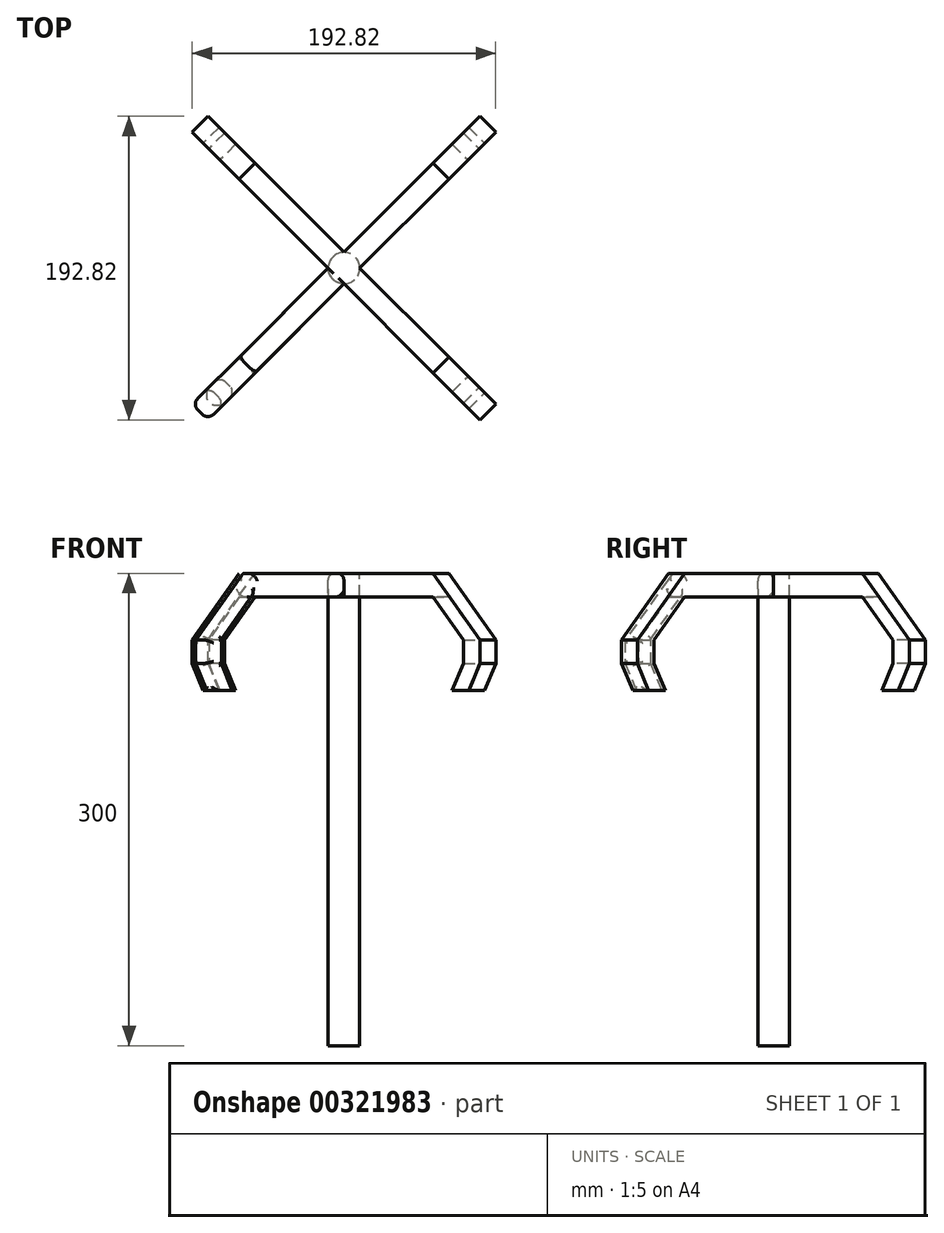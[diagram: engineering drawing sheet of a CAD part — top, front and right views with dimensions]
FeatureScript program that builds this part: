
annotation { "Feature Type Name" : "Feature", "Feature Type Description" : "" }
export const myFeature = defineFeature(function(context is Context, id is Id, definition is map)
    precondition{}
    {
        {
            var Q0;
            Q0=qCreatedBy(makeId("Top.planeOp"),FACE);
            var sketch = newSketch(context, id + "F0", { "sketchPlane" : qUnion([Q0])});
            skCircle(sketch, "E0", {"center": v(0, 0) * mm, "radius": 10 * mm});
            skSolve(sketch);
        }
        {
            var Q0;
            Q0 = qSketchRegion(id + "F0", true);
            extrude(context, id + "F1", {"entities" : qUnion([Q0]), "depth" : 300 * mm});
        }
        {
            var Q0;
            Q0=makeQuery(id+"F1.opExtrude","CAP_FACE",FACE,{"disambiguationData":[OSD([sQuery(id+"F0.wireOp",EDGE,"E0")])],"isStart":false});
            var sketch = newSketch(context, id + "F2", { "sketchPlane" : qUnion([Q0])});
            skLineSegment(sketch, "E1.bottom", {"start": v(10, 10) * mm, "end": v(-10, 10) * mm});
            skLineSegment(sketch, "E1.top", {"start": v(10, -10) * mm, "end": v(-10, -10) * mm});
            skLineSegment(sketch, "E1.left", {"start": v(10, 10) * mm, "end": v(10, -10) * mm});
            skLineSegment(sketch, "E1.right", {"start": v(-10, 10) * mm, "end": v(-10, -10) * mm});
            skPoint(sketch, "E1.middle", {"position": v(0, 0) * mm});
            skLineSegment(sketch, "E2", {"start": v(0, -10) * mm, "end": v(-56.57, -66.57) * mm});
            skLineSegment(sketch, "E3", {"start": v(-56.57, -66.57) * mm, "end": v(-66.57, -56.57) * mm});
            skLineSegment(sketch, "E4", {"start": v(-66.57, -56.57) * mm, "end": v(-10, 0) * mm});
            skLineSegment(sketch, "E5", {"start": v(-10, 0) * mm, "end": v(-66.57, 56.57) * mm});
            skLineSegment(sketch, "E6", {"start": v(-66.57, 56.57) * mm, "end": v(-56.57, 66.57) * mm});
            skLineSegment(sketch, "E7", {"start": v(-56.57, 66.57) * mm, "end": v(0, 10) * mm});
            skLineSegment(sketch, "E8", {"start": v(0, 10) * mm, "end": v(56.57, 66.57) * mm});
            skLineSegment(sketch, "E9", {"start": v(56.57, 66.57) * mm, "end": v(66.57, 56.57) * mm});
            skLineSegment(sketch, "E10", {"start": v(66.57, 56.57) * mm, "end": v(10, 0) * mm});
            skLineSegment(sketch, "E11", {"start": v(10, 0) * mm, "end": v(66.57, -56.57) * mm});
            skLineSegment(sketch, "E12", {"start": v(66.57, -56.57) * mm, "end": v(56.57, -66.57) * mm});
            skLineSegment(sketch, "E13", {"start": v(56.57, -66.57) * mm, "end": v(0, -10) * mm});
            skSolve(sketch);
        }
        {
            var Q0;
            Q0 = qSketchRegion(id + "F2", true);
            extrude(context, id + "F3", {"entities" : qUnion([Q0]), "operationType" : NewBodyOperationType.ADD, "oppositeDirection" : true, "depth" : 15 * mm});
        }
        {
            var Q0;
            Q0=makeQuery(id+"F3.opExtrude","SWEPT_FACE",FACE,{"disambiguationData":[OSD([sQuery(id+"F2.wireOp",EDGE,"E10")])]});
            var sketch = newSketch(context, id + "F4", { "sketchPlane" : qUnion([Q0])});
            skLineSegment(sketch, "E14", {"start": v(87.07, 300) * mm, "end": v(87.07, 285) * mm});
            skLineSegment(sketch, "E15", {"start": v(87.07, 285) * mm, "end": v(114.28, 257.8) * mm});
            skLineSegment(sketch, "E16", {"start": v(114.28, 257.8) * mm, "end": v(114.28, 242.8) * mm});
            skLineSegment(sketch, "E17", {"start": v(114.28, 242.8) * mm, "end": v(129.28, 242.8) * mm});
            skLineSegment(sketch, "E18", {"start": v(129.28, 242.8) * mm, "end": v(129.28, 257.8) * mm});
            skLineSegment(sketch, "E19", {"start": v(129.28, 257.8) * mm, "end": v(87.07, 300) * mm});
            skLineSegment(sketch, "E20", {"start": v(129.28, 242.8) * mm, "end": v(119.3, 225.52) * mm});
            skLineSegment(sketch, "E21", {"start": v(119.3, 225.52) * mm, "end": v(104.3, 225.52) * mm});
            skLineSegment(sketch, "E22", {"start": v(104.3, 225.52) * mm, "end": v(114.28, 242.8) * mm});
            skSolve(sketch);
        }
        {
            var Q0;
            Q0=makeQuery(id+"F4.imprint","IMPRINT",FACE,{"disambiguationData":[TD([[makeQuery(id+"F4.imprint","IMPRINT",EDGE,{"derivedFrom":sQuery(id+"F4.wireOp",EDGE,"E14")}),-1.0]])]});
            var Q1;
            Q1=makeQuery(id+"F4.imprint","IMPRINT",FACE,{"disambiguationData":[TD([[makeQuery(id+"F4.imprint","IMPRINT",EDGE,{"derivedFrom":sQuery(id+"F4.wireOp",EDGE,"E17")}),-1.0]])]});
            extrude(context, id + "F5", {"entities" : qUnion([Q0, Q1]), "operationType" : NewBodyOperationType.ADD, "oppositeDirection" : true, "depth" : 14.14 * mm});
        }
        {
            var Q0;
            Q0=makeQuery(id+"F1.opExtrude","SWEPT_BODY",BODY,{"disambiguationData":[OSD([sQuery(id+"F0.wireOp",EDGE,"E0")])]});
            var Q1;
            Q1=qCreatedBy(makeId("Front.planeOp"),FACE);
            mirror(context, id + "F6", {"operationType" : NewBodyOperationType.ADD, "entities" : qUnion([Q0]), "mirrorPlane" : qUnion([Q1])});
        }
        {
            var Q0;
            Q0=makeQuery(id+"F1.opExtrude","SWEPT_BODY",BODY,{"disambiguationData":[OSD([sQuery(id+"F0.wireOp",EDGE,"E0")])]});
            var Q1;
            Q1=qCreatedBy(makeId("Right.planeOp"),FACE);
            mirror(context, id + "F7", {"operationType" : NewBodyOperationType.ADD, "entities" : qUnion([Q0]), "mirrorPlane" : qUnion([Q1])});
        }
        {
            var Q0;
            Q0=makeQuery(id+"F3.opExtrude","CAP_EDGE",EDGE,{"disambiguationData":[OSD([sQuery(id+"F2.wireOp",EDGE,"E2")])],"isStart":true});
            var Q1;
            Q1=makeQuery(id+"F7.opPattern","COPY",EDGE,{"derivedFrom":makeQuery(id+"F6.opPattern","COPY",EDGE,{"derivedFrom":makeQuery(id+"F5.opExtrude","CAP_EDGE",EDGE,{"disambiguationData":[OSD([sQuery(id+"F4.wireOp",EDGE,"E19")])],"isStart":false}),"instanceName":"1"}),"instanceName":"1"});
            var Q2;
            Q2=makeQuery(id+"F7.opPattern","COPY",EDGE,{"derivedFrom":makeQuery(id+"F6.opPattern","COPY",EDGE,{"derivedFrom":makeQuery(id+"F5.opExtrude","CAP_EDGE",EDGE,{"disambiguationData":[OSD([sQuery(id+"F4.wireOp",EDGE,"E18")])],"isStart":false}),"instanceName":"1"}),"instanceName":"1"});
            var Q3;
            Q3=makeQuery(id+"F7.opPattern","COPY",EDGE,{"derivedFrom":makeQuery(id+"F6.opPattern","COPY",EDGE,{"derivedFrom":makeQuery(id+"F5.opExtrude","CAP_EDGE",EDGE,{"disambiguationData":[OSD([sQuery(id+"F4.wireOp",EDGE,"E20")])],"isStart":false}),"instanceName":"1"}),"instanceName":"1"});
            var Q4;
            Q4=makeQuery(id+"F3.opExtrude","CAP_EDGE",EDGE,{"disambiguationData":[OSD([sQuery(id+"F2.wireOp",EDGE,"E2")])],"isStart":false});
            var Q5;
            Q5=makeQuery(id+"F7.opPattern","COPY",EDGE,{"derivedFrom":makeQuery(id+"F6.opPattern","COPY",EDGE,{"derivedFrom":makeQuery(id+"F5.opExtrude","CAP_EDGE",EDGE,{"disambiguationData":[OSD([sQuery(id+"F4.wireOp",EDGE,"E15")])],"isStart":false}),"instanceName":"1"}),"instanceName":"1"});
            var Q6;
            Q6=makeQuery(id+"F7.opPattern","COPY",EDGE,{"derivedFrom":makeQuery(id+"F6.opPattern","COPY",EDGE,{"derivedFrom":makeQuery(id+"F5.opExtrude","CAP_EDGE",EDGE,{"disambiguationData":[OSD([sQuery(id+"F4.wireOp",EDGE,"E16")])],"isStart":false}),"instanceName":"1"}),"instanceName":"1"});
            var Q7;
            Q7=makeQuery(id+"F7.opPattern","COPY",EDGE,{"derivedFrom":makeQuery(id+"F6.opPattern","COPY",EDGE,{"derivedFrom":makeQuery(id+"F5.opExtrude","CAP_EDGE",EDGE,{"disambiguationData":[OSD([sQuery(id+"F4.wireOp",EDGE,"E22")])],"isStart":false}),"instanceName":"1"}),"instanceName":"1"});
            var Q8;
            Q8=makeQuery(id+"F7.opPattern","COPY",EDGE,{"derivedFrom":makeQuery(id+"F6.opPattern","COPY",EDGE,{"derivedFrom":makeQuery(id+"F5.opExtrude","SWEPT_EDGE",EDGE,{"disambiguationData":[OSD([sQuery(id+"F4.wireOp",EDGE,"E20"),sQuery(id+"F4.wireOp",EDGE,"E21")])]}),"instanceName":"1"}),"instanceName":"1"});
            var Q9;
            Q9=makeQuery(id+"F7.opPattern","COPY",EDGE,{"derivedFrom":makeQuery(id+"F6.opPattern","COPY",EDGE,{"derivedFrom":makeQuery(id+"F5.opExtrude","CAP_EDGE",EDGE,{"disambiguationData":[OSD([sQuery(id+"F4.wireOp",EDGE,"E19")])],"isStart":true}),"instanceName":"1"}),"instanceName":"1"});
            var Q10;
            Q10=makeQuery(id+"F7.opPattern","COPY",EDGE,{"derivedFrom":makeQuery(id+"F6.opPattern","COPY",EDGE,{"derivedFrom":makeQuery(id+"F5.opExtrude","CAP_EDGE",EDGE,{"disambiguationData":[OSD([sQuery(id+"F4.wireOp",EDGE,"E18")])],"isStart":true}),"instanceName":"1"}),"instanceName":"1"});
            var Q11;
            Q11=makeQuery(id+"F7.opPattern","COPY",EDGE,{"derivedFrom":makeQuery(id+"F6.opPattern","COPY",EDGE,{"derivedFrom":makeQuery(id+"F5.opExtrude","CAP_EDGE",EDGE,{"disambiguationData":[OSD([sQuery(id+"F4.wireOp",EDGE,"E20")])],"isStart":true}),"instanceName":"1"}),"instanceName":"1"});
            var Q12;
            Q12=makeQuery(id+"F7.opPattern","COPY",EDGE,{"derivedFrom":makeQuery(id+"F6.opPattern","COPY",EDGE,{"derivedFrom":makeQuery(id+"F5.opExtrude","CAP_EDGE",EDGE,{"disambiguationData":[OSD([sQuery(id+"F4.wireOp",EDGE,"E16")])],"isStart":true}),"instanceName":"1"}),"instanceName":"1"});
            var Q13;
            Q13=makeQuery(id+"F7.opPattern","COPY",EDGE,{"derivedFrom":makeQuery(id+"F6.opPattern","COPY",EDGE,{"derivedFrom":makeQuery(id+"F5.opExtrude","CAP_EDGE",EDGE,{"disambiguationData":[OSD([sQuery(id+"F4.wireOp",EDGE,"E15")])],"isStart":true}),"instanceName":"1"}),"instanceName":"1"});
            var Q14;
            Q14=makeQuery(id+"F3.opExtrude","CAP_EDGE",EDGE,{"disambiguationData":[OSD([sQuery(id+"F2.wireOp",EDGE,"E4")])],"isStart":false});
            var Q15;
            Q15=makeQuery(id+"F7.opPattern","COPY",EDGE,{"derivedFrom":makeQuery(id+"F6.opPattern","COPY",EDGE,{"derivedFrom":makeQuery(id+"F5.opExtrude","CAP_EDGE",EDGE,{"disambiguationData":[OSD([sQuery(id+"F4.wireOp",EDGE,"E22")])],"isStart":true}),"instanceName":"1"}),"instanceName":"1"});
            var Q16;
            Q16=makeQuery(id+"F3.opExtrude","CAP_EDGE",EDGE,{"disambiguationData":[OSD([sQuery(id+"F2.wireOp",EDGE,"E4")])],"isStart":true});
            fillet(context, id + "F8", {"entities" : qUnion([Q0, Q1, Q2, Q3, Q4, Q5, Q6, Q7, Q8, Q9, Q10, Q11, Q12, Q13, Q14, Q15, Q16]), "radius" : 5 * mm, "tangentPropagation" : true, "allowEdgeOverflow" : false});
        }
    });
